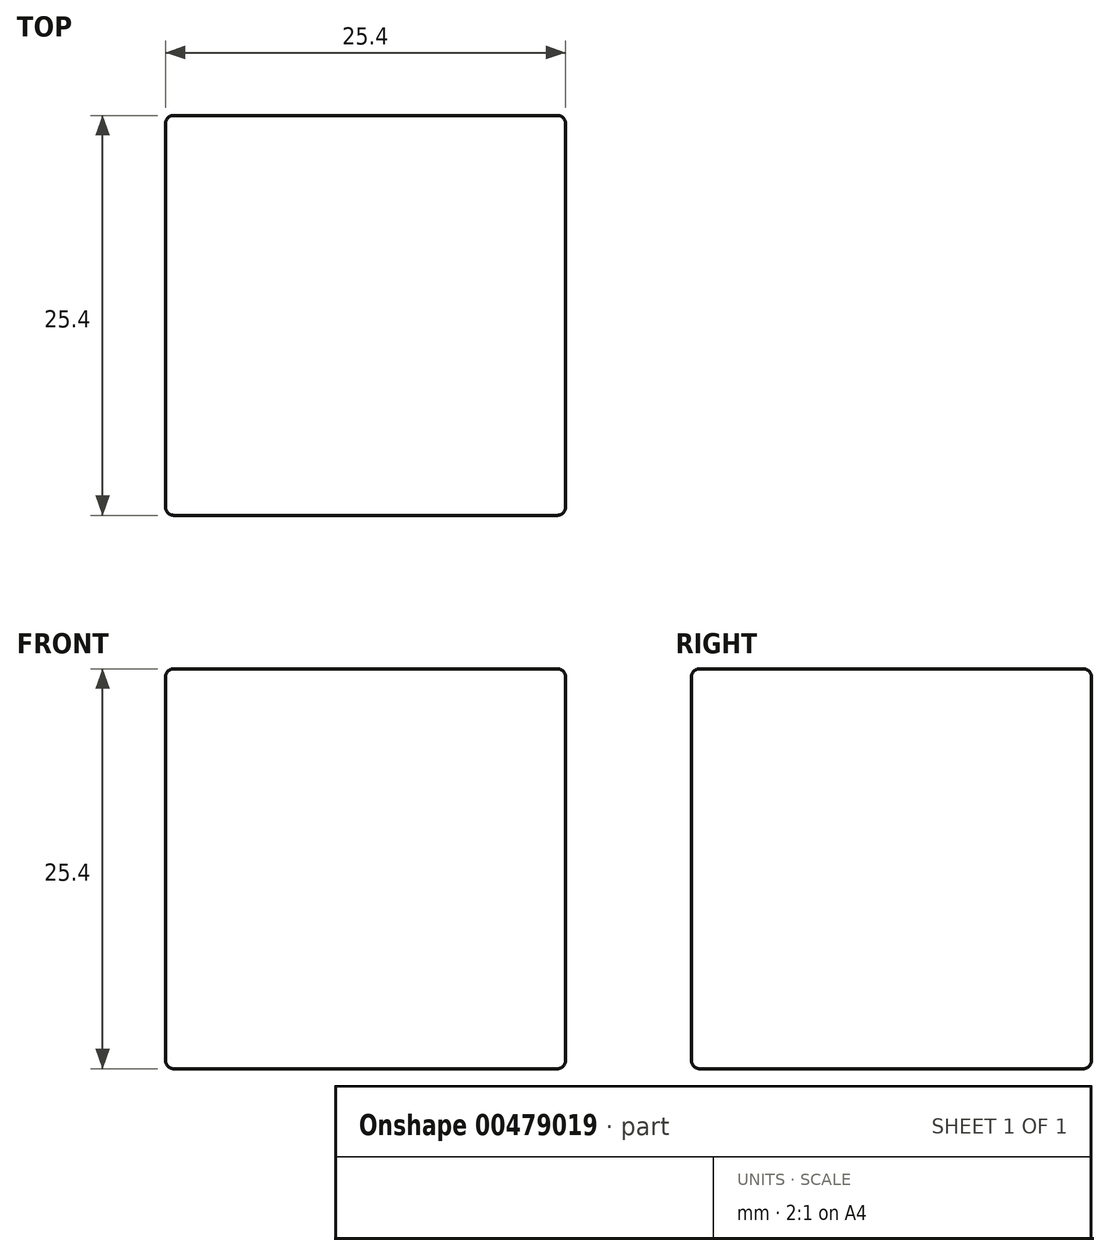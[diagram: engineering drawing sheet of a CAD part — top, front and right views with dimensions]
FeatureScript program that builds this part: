
annotation { "Feature Type Name" : "Feature", "Feature Type Description" : "" }
export const myFeature = defineFeature(function(context is Context, id is Id, definition is map)
    precondition{}
    {
        {
            var Q0;
            Q0=qCreatedBy(makeId("Front.planeOp"),FACE);
            var sketch = newSketch(context, id + "F0", { "sketchPlane" : qUnion([Q0])});
            skLineSegment(sketch, "E0.bottom", {"start": v(0, 0) * mm, "end": v(25.4, 0) * mm});
            skLineSegment(sketch, "E0.top", {"start": v(0, 25.4) * mm, "end": v(25.4, 25.4) * mm});
            skLineSegment(sketch, "E0.left", {"start": v(0, 0) * mm, "end": v(0, 25.4) * mm});
            skLineSegment(sketch, "E0.right", {"start": v(25.4, 0) * mm, "end": v(25.4, 25.4) * mm});
            skSolve(sketch);
        }
        {
            var Q0;
            Q0=makeQuery(id+"F0.imprint","IMPRINT",FACE,{"disambiguationData":[TD([[makeQuery(id+"F0.imprint","IMPRINT",EDGE,{"derivedFrom":sQuery(id+"F0.wireOp",EDGE,"E0.bottom")}),1.0]])]});
            extrude(context, id + "F1", {"entities" : qUnion([Q0]), "depth" : 25.4 * mm});
        }
        {
            var Q0;
            Q0=makeQuery(id+"F1.opExtrude","SWEPT_FACE",FACE,{"disambiguationData":[OSD([sQuery(id+"F0.wireOp",EDGE,"E0.top")])]});
            var Q1;
            Q1=makeQuery(id+"F1.opExtrude","CAP_FACE",FACE,{"disambiguationData":[OSD([sQuery(id+"F0.wireOp",EDGE,"E0.bottom"),sQuery(id+"F0.wireOp",EDGE,"E0.top"),sQuery(id+"F0.wireOp",EDGE,"E0.left"),sQuery(id+"F0.wireOp",EDGE,"E0.right")])],"isStart":false});
            var Q2;
            Q2=makeQuery(id+"F1.opExtrude","SWEPT_FACE",FACE,{"disambiguationData":[OSD([sQuery(id+"F0.wireOp",EDGE,"E0.right")])]});
            var Q3;
            Q3=makeQuery(id+"F1.opExtrude","CAP_FACE",FACE,{"disambiguationData":[OSD([sQuery(id+"F0.wireOp",EDGE,"E0.bottom"),sQuery(id+"F0.wireOp",EDGE,"E0.top"),sQuery(id+"F0.wireOp",EDGE,"E0.left"),sQuery(id+"F0.wireOp",EDGE,"E0.right")])],"isStart":true});
            var Q4;
            Q4=makeQuery(id+"F1.opExtrude","SWEPT_FACE",FACE,{"disambiguationData":[OSD([sQuery(id+"F0.wireOp",EDGE,"E0.bottom")])]});
            var Q5;
            Q5=makeQuery(id+"F1.opExtrude","SWEPT_FACE",FACE,{"disambiguationData":[OSD([sQuery(id+"F0.wireOp",EDGE,"E0.left")])]});
            fillet(context, id + "F2", {"entities" : qUnion([Q0, Q1, Q2, Q3, Q4, Q5]), "radius" : 0.5 * mm, "tangentPropagation" : true, "allowEdgeOverflow" : false});
        }
    });
